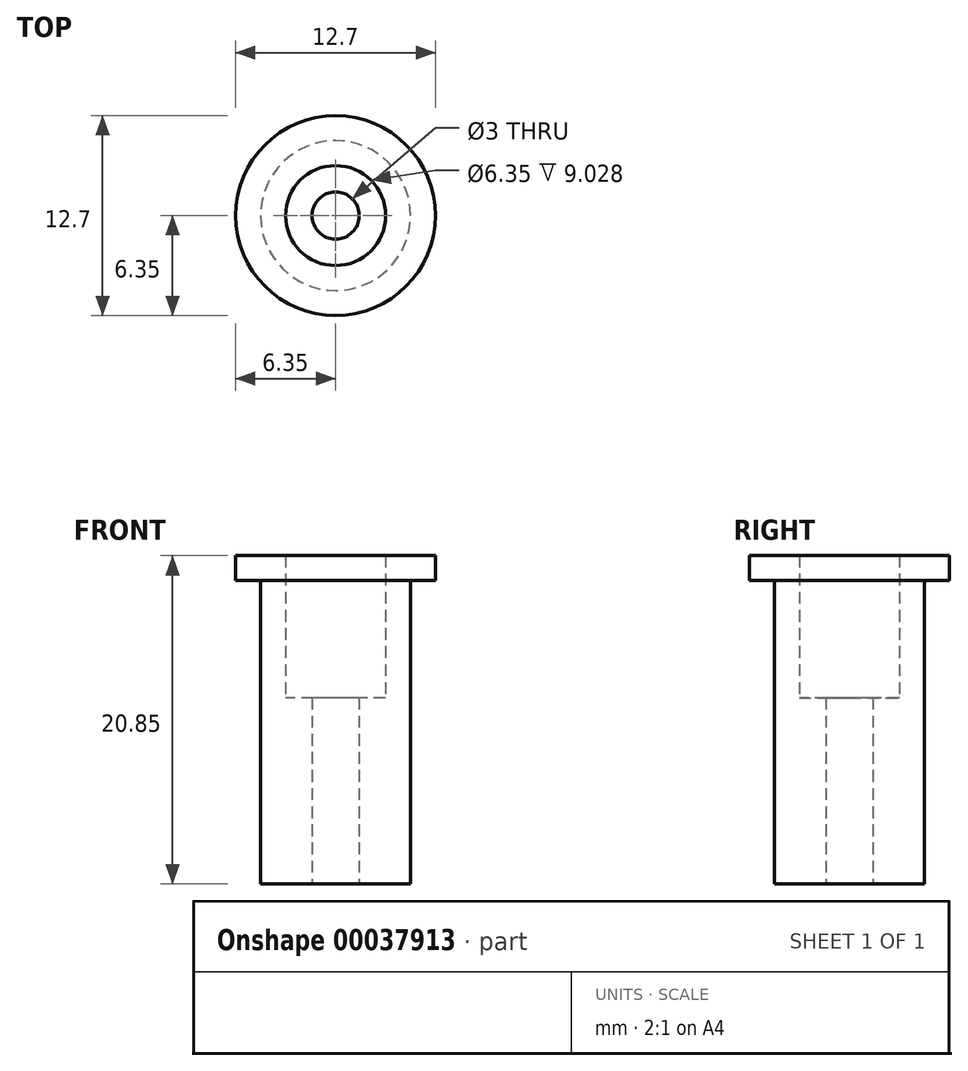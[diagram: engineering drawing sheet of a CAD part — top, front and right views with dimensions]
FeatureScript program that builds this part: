
annotation { "Feature Type Name" : "Feature", "Feature Type Description" : "" }
export const myFeature = defineFeature(function(context is Context, id is Id, definition is map)
    precondition{}
    {
        {
            var Q0;
            Q0=qCreatedBy(makeId("Top.planeOp"),FACE);
            var sketch = newSketch(context, id + "F0", { "sketchPlane" : qUnion([Q0])});
            skCircle(sketch, "E0", {"center": v(0, 0) * mm, "radius": 1.5 * mm});
            skCircle(sketch, "E1", {"center": v(0, 0) * mm, "radius": 4.76 * mm});
            skSolve(sketch);
        }
        {
            var Q0;
            Q0=qSketchRegion(id+"F0",true);
            extrude(context, id + "F1", {"entities" : qUnion([Q0]), "depth" : 11.83 * mm});
        }
        {
            var Q0;
            Q0=makeQuery(id+"F1.opExtrude","CAP_FACE",FACE,{"disambiguationData":[OSD([sQuery(id+"F0.wireOp",EDGE,"E0"),sQuery(id+"F0.wireOp",EDGE,"E1")])],"isStart":false});
            var sketch = newSketch(context, id + "F2", { "sketchPlane" : qUnion([Q0])});
            skCircle(sketch, "E2", {"center": v(0, 0) * mm, "radius": 3.18 * mm});
            skCircle(sketch, "E3", {"center": v(0, 0) * mm, "radius": 4.76 * mm});
            skSolve(sketch);
        }
        {
            var Q0;
            Q0=qSketchRegion(id+"F2",true);
            extrude(context, id + "F3", {"entities" : qUnion([Q0]), "operationType" : NewBodyOperationType.ADD, "depth" : 7.44 * mm});
        }
        {
            var Q0;
            Q0=makeQuery(id+"F3.opExtrude","CAP_FACE",FACE,{"disambiguationData":[OSD([sQuery(id+"F2.wireOp",EDGE,"E2"),sQuery(id+"F2.wireOp",EDGE,"E3")])],"isStart":false});
            var sketch = newSketch(context, id + "F4", { "sketchPlane" : qUnion([Q0])});
            skCircle(sketch, "E4", {"center": v(0, 0) * mm, "radius": 6.35 * mm});
            skCircle(sketch, "E5", {"center": v(0, 0) * mm, "radius": 3.18 * mm});
            skSolve(sketch);
        }
        {
            var Q0;
            Q0=qSketchRegion(id+"F4",true);
            extrude(context, id + "F5", {"entities" : qUnion([Q0]), "operationType" : NewBodyOperationType.ADD, "depth" : 1.59 * mm});
        }
    });
